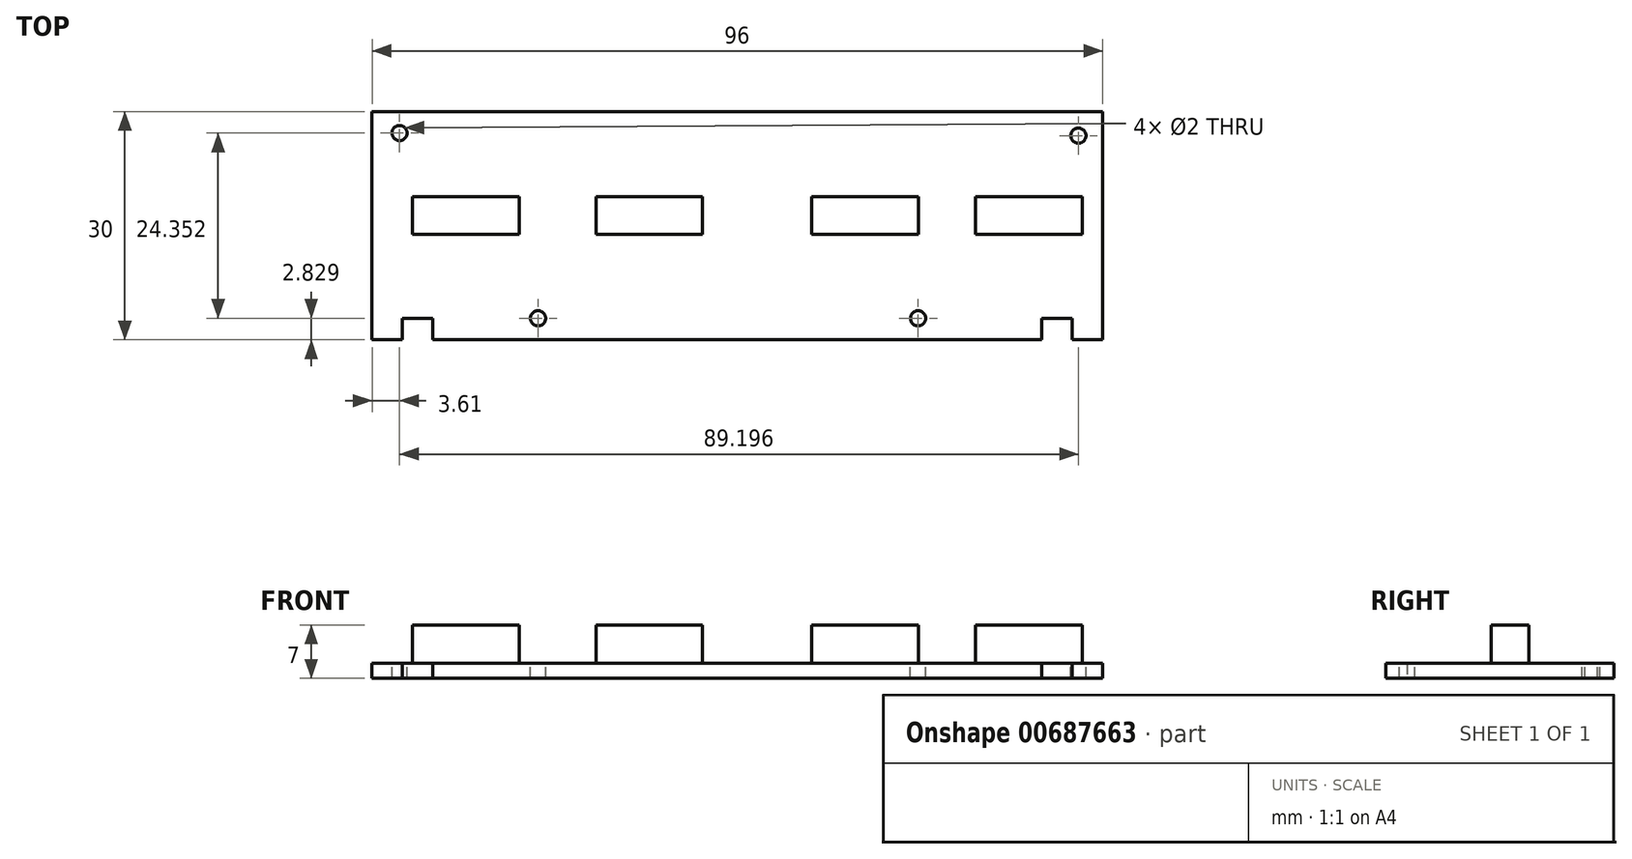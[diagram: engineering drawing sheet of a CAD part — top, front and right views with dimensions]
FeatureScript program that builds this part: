
annotation { "Feature Type Name" : "Feature", "Feature Type Description" : "" }
export const myFeature = defineFeature(function(context is Context, id is Id, definition is map)
    precondition{}
    {
        {
            var Q0;
            Q0=qCreatedBy(makeId("Top.planeOp"),FACE);
            var sketch = newSketch(context, id + "F0", { "sketchPlane" : qUnion([Q0])});
            skLineSegment(sketch, "E0", {"start": v(-52.1, 16.15) * mm, "end": v(-52.1, -13.85) * mm});
            skLineSegment(sketch, "E1", {"start": v(-52.1, -13.85) * mm, "end": v(-48.1, -13.85) * mm});
            skLineSegment(sketch, "E2", {"start": v(-48.1, -13.85) * mm, "end": v(-48.1, -11.02) * mm});
            skLineSegment(sketch, "E3", {"start": v(-48.1, -11.02) * mm, "end": v(-44.1, -11.02) * mm});
            skLineSegment(sketch, "E4", {"start": v(-44.1, -11.02) * mm, "end": v(-44.1, -13.85) * mm});
            skLineSegment(sketch, "E5", {"start": v(-44.1, -13.85) * mm, "end": v(35.9, -13.85) * mm});
            skLineSegment(sketch, "E6", {"start": v(35.9, -13.85) * mm, "end": v(35.9, -11.02) * mm});
            skLineSegment(sketch, "E7", {"start": v(35.9, -11.02) * mm, "end": v(39.9, -11.02) * mm});
            skLineSegment(sketch, "E8", {"start": v(39.9, -11.02) * mm, "end": v(39.9, -13.85) * mm});
            skLineSegment(sketch, "E9", {"start": v(39.9, -13.85) * mm, "end": v(43.9, -13.85) * mm});
            skLineSegment(sketch, "E10", {"start": v(43.9, -13.85) * mm, "end": v(43.9, 16.15) * mm});
            skLineSegment(sketch, "E11", {"start": v(43.9, 16.15) * mm, "end": v(-52.1, 16.15) * mm});
            skSolve(sketch);
        }
        {
            var Q0;
            Q0 = qSketchRegion(id + "F0", true);
            extrude(context, id + "F1", {"entities" : qUnion([Q0]), "depth" : 2 * mm, "offsetDistance" : 25 * mm});
        }
        {
            var Q0;
            Q0=makeQuery(id+"F1.opExtrude","CAP_FACE",FACE,{"disambiguationData":[OSD([sQuery(id+"F0.wireOp",EDGE,"E0"),sQuery(id+"F0.wireOp",EDGE,"E1"),sQuery(id+"F0.wireOp",EDGE,"E2"),sQuery(id+"F0.wireOp",EDGE,"E3"),sQuery(id+"F0.wireOp",EDGE,"E4"),sQuery(id+"F0.wireOp",EDGE,"E5"),sQuery(id+"F0.wireOp",EDGE,"E6"),sQuery(id+"F0.wireOp",EDGE,"E7"),sQuery(id+"F0.wireOp",EDGE,"E8"),sQuery(id+"F0.wireOp",EDGE,"E9"),sQuery(id+"F0.wireOp",EDGE,"E10"),sQuery(id+"F0.wireOp",EDGE,"E11")])],"isStart":false});
            var sketch = newSketch(context, id + "F2", { "sketchPlane" : qUnion([Q0])});
            skLineSegment(sketch, "E12.bottom", {"start": v(-46.78, 5) * mm, "end": v(-32.78, 5) * mm});
            skLineSegment(sketch, "E12.top", {"start": v(-46.78, 0) * mm, "end": v(-32.78, 0) * mm});
            skLineSegment(sketch, "E12.left", {"start": v(-46.78, 5) * mm, "end": v(-46.78, 0) * mm});
            skLineSegment(sketch, "E12.right", {"start": v(-32.78, 5) * mm, "end": v(-32.78, 0) * mm});
            skLineSegment(sketch, "E13.bottom", {"start": v(-22.67, 5) * mm, "end": v(-8.67, 5) * mm});
            skLineSegment(sketch, "E13.top", {"start": v(-22.67, 0) * mm, "end": v(-8.67, 0) * mm});
            skLineSegment(sketch, "E13.left", {"start": v(-22.67, 5) * mm, "end": v(-22.67, 0) * mm});
            skLineSegment(sketch, "E13.right", {"start": v(-8.67, 5) * mm, "end": v(-8.67, 0) * mm});
            skLineSegment(sketch, "E14.bottom", {"start": v(5.68, 5) * mm, "end": v(19.68, 5) * mm});
            skLineSegment(sketch, "E14.top", {"start": v(5.68, 0) * mm, "end": v(19.68, 0) * mm});
            skLineSegment(sketch, "E14.left", {"start": v(5.68, 5) * mm, "end": v(5.68, 0) * mm});
            skLineSegment(sketch, "E14.right", {"start": v(19.68, 5) * mm, "end": v(19.68, 0) * mm});
            skLineSegment(sketch, "E15.bottom", {"start": v(27.2, 5) * mm, "end": v(41.2, 5) * mm});
            skLineSegment(sketch, "E15.top", {"start": v(27.2, 0) * mm, "end": v(41.2, 0) * mm});
            skLineSegment(sketch, "E15.left", {"start": v(27.2, 5) * mm, "end": v(27.2, 0) * mm});
            skLineSegment(sketch, "E15.right", {"start": v(41.2, 5) * mm, "end": v(41.2, 0) * mm});
            skSolve(sketch);
        }
        {
            var Q0;
            Q0 = qSketchRegion(id + "F2", true);
            extrude(context, id + "F3", {"entities" : qUnion([Q0]), "operationType" : NewBodyOperationType.ADD, "depth" : 5 * mm, "offsetDistance" : 25 * mm});
        }
        {
            var Q0;
            Q0=makeQuery(id+"F1.opExtrude","CAP_FACE",FACE,{"disambiguationData":[OSD([sQuery(id+"F0.wireOp",EDGE,"E0"),sQuery(id+"F0.wireOp",EDGE,"E1"),sQuery(id+"F0.wireOp",EDGE,"E2"),sQuery(id+"F0.wireOp",EDGE,"E3"),sQuery(id+"F0.wireOp",EDGE,"E4"),sQuery(id+"F0.wireOp",EDGE,"E5"),sQuery(id+"F0.wireOp",EDGE,"E6"),sQuery(id+"F0.wireOp",EDGE,"E7"),sQuery(id+"F0.wireOp",EDGE,"E8"),sQuery(id+"F0.wireOp",EDGE,"E9"),sQuery(id+"F0.wireOp",EDGE,"E10"),sQuery(id+"F0.wireOp",EDGE,"E11")])],"isStart":false});
            var sketch = newSketch(context, id + "F4", { "sketchPlane" : qUnion([Q0])});
            skCircle(sketch, "E16", {"center": v(-48.48, 13.33) * mm, "radius": 1 * mm});
            skCircle(sketch, "E17", {"center": v(40.72, 13) * mm, "radius": 1 * mm});
            skCircle(sketch, "E18", {"center": v(19.65, -11.02) * mm, "radius": 1 * mm});
            skCircle(sketch, "E19", {"center": v(-30.29, -11.02) * mm, "radius": 1 * mm});
            skSolve(sketch);
        }
        {
            var Q0;
            Q0 = qSketchRegion(id + "F4", true);
            extrude(context, id + "F5", {"entities" : qUnion([Q0]), "operationType" : NewBodyOperationType.REMOVE, "oppositeDirection" : true, "depth" : 25 * mm, "offsetDistance" : 25 * mm});
        }
    });
